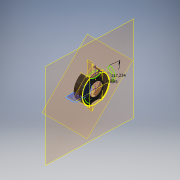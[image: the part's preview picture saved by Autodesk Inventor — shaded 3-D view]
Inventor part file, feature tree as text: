
AUTODESK INVENTOR PART (.ipt)
format: ipt  version: 2020 (Build 240168000, 168)  size: 550,912 bytes
history: native  units: mm
features: other x32, extrude x12, sketch x11, reference x7, projected_geometry x3, revolve x1, mirror x1
ambient origin geometry x8: Origin, YZ Plane, XZ Plane, XY Plane, X Axis, Y Axis, Z Axis, Center Point
bodies: Body1 (feature_tree)
feature tree (67):
  other  "Твердое тело1"
  other  "РабПлоскость26"
  sketch  "Эскиз2"
  other  "РабПлоскость21"
  sketch  "Эскиз5"
  other  "РабОсь1"
  revolve  "Вращение1"
  other  "РабПлоскость27"
  extrude  "Выдавливание1"  TaperAngle=90.0deg  [1 undecoded]
  other  "РабПлоскость5"
  other  "РабПлоскость9"
  other  "РабПлоскость11"
  sketch  "Эскиз7"
  other  "РабТочка9"
  extrude  "Выдавливание3"  Depth=10.0mm TaperAngle=0.0deg
  other  "РабПлоскость22"
  extrude  "Выдавливание4"  Depth=2.5mm
  other  "РабОсь2"
  other  "РабПлоскость23"
  extrude  "Выдавливание6"  Depth=2.0mm
  other  "РабПлоскость24"
  sketch  "Эскиз11"
  other  "РабПлоскость25"
  other  "РабПлоскость13"
  other  "РабПлоскость14"
  extrude  "Выдавливание7"  Depth=3.0mm
  extrude  "Выдавливание8"  Depth=10.0mm TaperAngle=0.0deg
  other  "РабПлоскость15"
  other  "РабПлоскость16"
  extrude  "Выдавливание9"  Depth=10.0mm TaperAngle=0.0deg
  other  "РабПлоскость17"
  extrude  "Выдавливание10"  Depth=7.0mm
  other  "РабПлоскость18"
  sketch  "Эскиз17"
  other  "РабПлоскость19"
  extrude  "Выдавливание11"  Depth=0.4mm
  extrude  "Выдавливание12"  Depth=10.0mm TaperAngle=0.0deg
  mirror  "Зеркальное отражение2"
  extrude  "Выдавливание13"  Depth=10.0mm TaperAngle=0.0deg
  extrude  "Выдавливание14"  TaperAngle=0.0deg  [1 undecoded]
  other  "РабПлоскость20"
  sketch  "Эскиз22"
  other  "РабОсь3"
  sketch  "Эскиз6"
  projected_geometry  "Спроецированная петля1"
  sketch  "Эскиз8"
  sketch  "Эскиз15"
  reference  "Ссылка15"
  reference  "Ссылка16"
  sketch  "Эскиз16"
  reference  "Ссылка17"
  reference  "Ссылка18"
  reference  "Ссылка20"
  reference  "Ссылка21"
  reference  "Ссылка22"
  sketch  "Эскиз18"
  projected_geometry  "Спроецированная петля3"
  projected_geometry  "Спроецированная петля4"
  parser-record x1  (decoder bookkeeping rows leaked as tree rows — omitted from the tree; the rows remain in map.json)
  other  "Omni_platform.iam"
  other  "SparkFun 9DoF Razor IMU:1"
  other  "MEGA 2560 PRO (EMBED):1"
  other  "Mega 2560 Pro - Board"
  other  "USB - Micro"
  other  "motherBoard_stend:1"
  other  "Board1.2:2"
  other  "floor:1"
note: 2 required parameter values undecoded (feature->parameter linkage not recoverable at this tier; creation-order binding heuristic only, values carry confidence <= 0.55)
note: 1 file-system path scrubbed to <path> (originals preserved in map.json)
